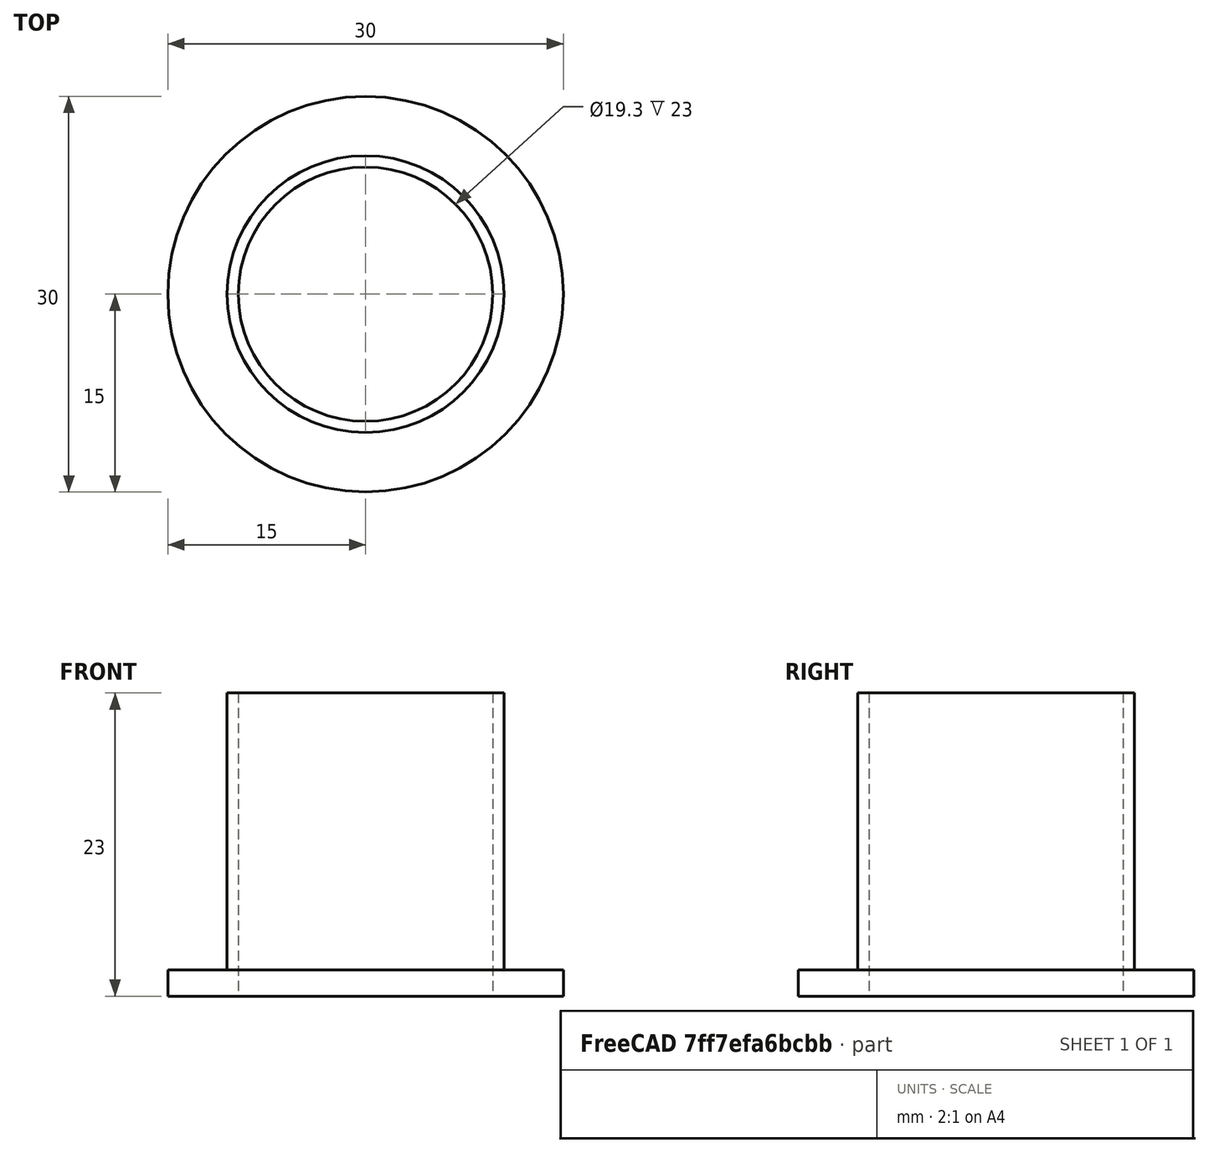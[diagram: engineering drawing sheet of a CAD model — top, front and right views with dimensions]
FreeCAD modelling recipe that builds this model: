
FCSTD DOCUMENT  (FreeCAD 0.19R24267 +148 (Git))
Label: BT20 Tube Cutter Guide
License: All rights reserved
LicenseURL: http://en.wikipedia.org/wiki/All_rights_reserved
objects: Sketcher::SketchObject×2, PartDesign::Pad×2, PartDesign::Hole×1, PartDesign::Body×1
note: 9 computed .brp shape members not serialized (recipe doc carries the construction recipe); baked Part::Feature solids carry a one-line shape summary decoded from their .brp

FEATURE [Sketcher::SketchObject] Sketch
  FullyConstrained = true
  MapMode = 5
  Support = -> [XY_Plane]
  sketch-geometry (1):
    g0: Circle CenterX=0 CenterY=0 CenterZ=0 NormalX=0 NormalY=0 NormalZ=1 AngleXU=0 Radius=15
  constraints (2):
    c: Coincident(g0,g-1)
    c: Diameter(g0) = 30
FEATURE [PartDesign::Pad] Pad
  Direction = (1,1,1)
  Length = 2
  Length2 = 100
  Profile = -> Sketch
  Type = 0
FEATURE [Sketcher::SketchObject] Sketch001
  FullyConstrained = false
  MapMode = 5
  Support = -> [XY_Plane]
  sketch-geometry (1):
    g0: Circle CenterX=0 CenterY=0 CenterZ=0 NormalX=0 NormalY=0 NormalZ=1 AngleXU=0 Radius=10.5
  constraints (1):
    c: Diameter(g0) = 21
FEATURE [PartDesign::Pad] Pad001
  BaseFeature = -> Pad
  Direction = (1,1,1)
  Length = 23
  Length2 = 100
  Profile = -> Sketch001
  Type = 0
FEATURE [PartDesign::Hole] Hole
  BaseFeature = -> Pad001
  Depth = 25
  DepthType = 0
  Diameter = 19.3
  DrillForDepth = false
  DrillPoint = 1
  DrillPointAngle = 118
  HoleCutCountersinkAngle = 90
  HoleCutCustomValues = false
  HoleCutDepth = 0
  HoleCutDiameter = 0
  HoleCutType = 0
  ModelActualThread = false
  Profile = -> Pad001 [Face6]
  Tapered = false
  TaperedAngle = 90
  ThreadAngle = 0
  ThreadClass = 0
  ThreadCutOffInner = 0
  ThreadCutOffOuter = 0
  ThreadDirection = 0
  ThreadFit = 0
  ThreadPitch = 0
  ThreadSize = 0
  ThreadType = 0
  Threaded = false
FEATURE [PartDesign::Body] Body
  Group = -> [Sketch,Pad,Sketch001,Pad001,Hole]
  Origin = -> Origin
  Tip = -> Hole
